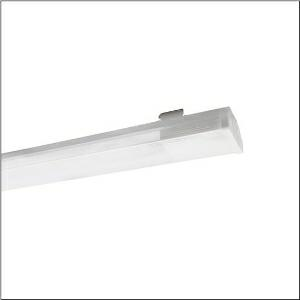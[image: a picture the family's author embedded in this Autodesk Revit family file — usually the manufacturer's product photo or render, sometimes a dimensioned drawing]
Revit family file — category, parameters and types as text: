
# Revit family: modario_31_gen_2_53bm813du4l3d2_2e27
name_source: partatom
category: Lighting Fixtures
units: mm (PartAtom-declared; Revit-internal decimal feet)

## family parameters
Cut with Voids When Loaded = No
Host = Face
Light Source = No
Part Type = Normal
Room Calculation Point = No
Round Connector Dimension = Use Diameter
Shared = No

## types (1)
- --- (1 x LED, 23060 lm, 128.4 W, 4000K)
    Apparent Load = 128 VA
    CIE Flux Codes = 62 83 95 93 100
    Color Rendering = 80
    Color Temperature = 4000K
    Default Elevation = 1800 mm
    Description = Modario 31 Gen.2, luminaire insert, of sheet steel, coil coated, white, length: 2.392mm, width: 81mm, height: 82mm, 8x system unit, system units: 299mm, LED rated luminous flux: 23.060lm, light colour: 840, SDCM (Standard Deviation of Colour Matching)MacAdam ≤ 3 SDCM (initial), control gear: DALI 2, control gear: ECG DALI, with plug, 5-pole, with phase selection, mains connection: 220..240V, AC, 50/60Hz, rated input power: 128W, through-wiring accessed according to module size, primary optical cover: cover, of PMMA, light emission: direct distribution, primary light characteristic: symmetric, protection rating (complete): IP20, protection rating (LED compartment): IP50, insulation class (complete): insulation class I (protective earthing), certification: CE, ENEC, VDE, UKCA, impact resistance: IK03, permissible ambient temperature for indoor applications: -40..+35°C, corresponds to IFS (International Featured Standards) requirements for safety and quality in the food industry, reducing of maximum allowable ambient temperature of 5°C with ceiling mounting, IP40 when using the optional accessory 5TP9018, packaging unit: 1 piece
    Height = 92 mm
    Lamp = 1 x LED
    Lamp Light Flux = 23060 lm
    Lamp Power = 128.4 W
    Lamp count = 1
    Length = 2392 mm
    Luminous efficacy = 180 lm/W
    Manufacturer = Siteco
    ModVariant = No
    Model = 53BM813DU4L3D2
    Mounting Place = Ceiling
    Mounting Type = Pendant
    Number of Poles = 1
    OnlyDefault = Yes
    Power Factor = 1
    Product Name = Modario 31 Gen.2
    Product group = luminaire insert | ceiling pendant
    ProductGroupID = 901
    Protection Class = Protection class I
    Protection Degree = IP 20
    RLX_Detail_Level = 1
    RLX_Emergency_Light_Flux = 0 lm
    RLX_Emergency_Type = 0
    RLX_Emergency_Type_DB = No
    RlxData = <blob elided: 38657 chars, md5=58c1d12f>
    Socket = socket
    Standby Power = 0 W
    System Light Flux = 23061 lm
    System Power = 128 W
    Type Comments = factory setting: luminous flux: 100 % | dim-lin: 254 | 594 mA
    Type Image = l_1341883.jpg
    URL = http://relux.com
    VarID = @adj_051355
    Voltage = 0 V
    Weight = 0.00 kg
    Width = 81 mm

## geometry (parser evidence)
native form markers: Blend x4, Sweep x10
no freeform markers — native parametric forms only
